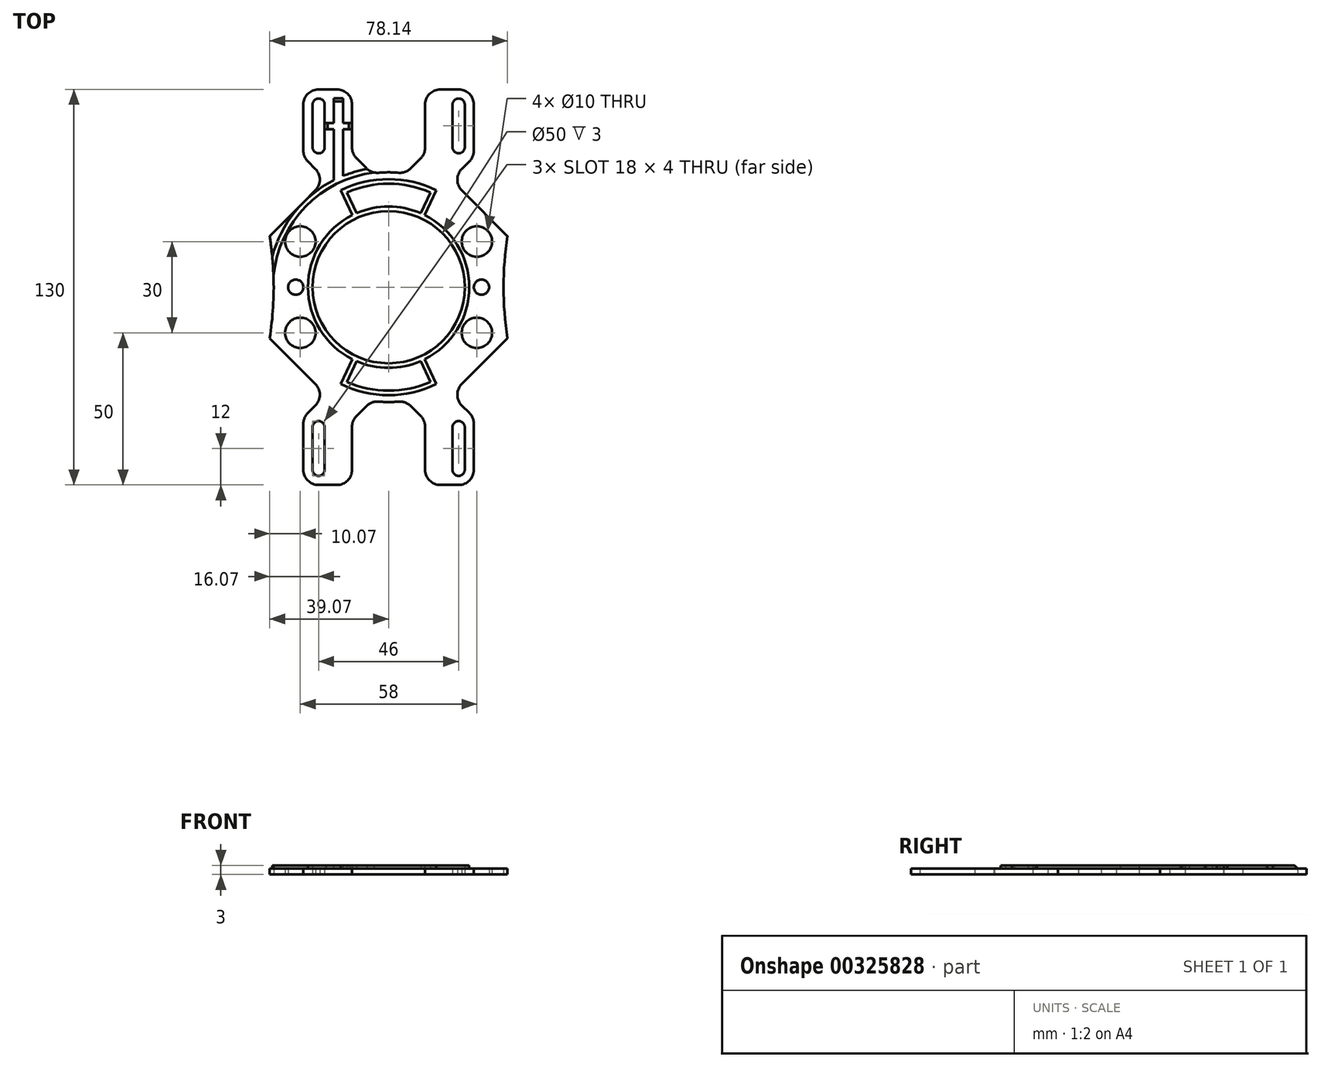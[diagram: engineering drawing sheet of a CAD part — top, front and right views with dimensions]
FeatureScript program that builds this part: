
annotation { "Feature Type Name" : "Feature", "Feature Type Description" : "" }
export const myFeature = defineFeature(function(context is Context, id is Id, definition is map)
    precondition{}
    {
        {
            var Q0;
            Q0=qCreatedBy(makeId("Top.planeOp"),FACE);
            var sketch = newSketch(context, id + "F0", { "sketchPlane" : qUnion([Q0])});
            skLineSegment(sketch, "E0.left", {"start": v(-2, 12.5) * mm, "end": v(-2, -12.5) * mm});
            skLineSegment(sketch, "E0.right", {"start": v(2, 12.5) * mm, "end": v(2, -12.5) * mm});
            skLineSegment(sketch, "E1", {"start": v(0, 0) * mm, "end": v(0, 81.3) * mm, "construction": true});
            skArc(sketch, "E2", {"start": v(2, 12.5) * mm, "mid": v(0, 14.5) * mm, "end": v(-2, 12.5) * mm});
            skArc(sketch, "E3", {"start": v(-2, -12.5) * mm, "mid": v(0, -14.5) * mm, "end": v(2, -12.5) * mm});
            skLineSegment(sketch, "E4", {"start": v(-106.98, 0) * mm, "end": v(54.3, 0) * mm, "construction": true});
            skLineSegment(sketch, "E5.left", {"start": v(-19, 9) * mm, "end": v(-19, -9) * mm});
            skLineSegment(sketch, "E5.right", {"start": v(-15, 9) * mm, "end": v(-15, -9) * mm});
            skArc(sketch, "E6", {"start": v(-15, 9) * mm, "mid": v(-17, 11) * mm, "end": v(-19, 9) * mm});
            skArc(sketch, "E7", {"start": v(-19, -9) * mm, "mid": v(-17, -11) * mm, "end": v(-15, -9) * mm});
            skArc(sketch, "E8.MirrorCS", {"start": v(19, -9) * mm, "mid": v(17, -11) * mm, "end": v(15, -9) * mm});
            skArc(sketch, "E9.MirrorCS", {"start": v(15, 9) * mm, "mid": v(17, 11) * mm, "end": v(19, 9) * mm});
            skLineSegment(sketch, "E10.MirrorCS", {"start": v(15, 9) * mm, "end": v(15, -9) * mm});
            skLineSegment(sketch, "E11.MirrorCS", {"start": v(19, 9) * mm, "end": v(19, -9) * mm});
            skCircle(sketch, "E12", {"center": v(-30.5, 0) * mm, "radius": 2.5 * mm});
            skCircle(sketch, "E13.MirrorC", {"center": v(30.5, 0) * mm, "radius": 2.5 * mm});
            skCircle(sketch, "E14", {"center": v(0, 29) * mm, "radius": 7.5 * mm});
            skCircle(sketch, "E15.MirrorC", {"center": v(0, -29) * mm, "radius": 7.5 * mm});
            skCircle(sketch, "E16", {"center": v(-29, 15) * mm, "radius": 5 * mm});
            skCircle(sketch, "E17.MirrorC", {"center": v(29, 15) * mm, "radius": 5 * mm});
            skCircle(sketch, "E18.MirrorC", {"center": v(-29, -15) * mm, "radius": 5 * mm});
            skCircle(sketch, "E19.MirrorC", {"center": v(29, -15) * mm, "radius": 5 * mm});
            skLineSegment(sketch, "E20.bottom", {"start": v(-4.5, 44) * mm, "end": v(4.5, 44) * mm});
            skLineSegment(sketch, "E20.top", {"start": v(-4.5, 42) * mm, "end": v(4.5, 42) * mm});
            skLineSegment(sketch, "E20.left", {"start": v(-4.5, 44) * mm, "end": v(-4.5, 42) * mm, "construction": true});
            skLineSegment(sketch, "E20.right", {"start": v(4.5, 44) * mm, "end": v(4.5, 42) * mm, "construction": true});
            skArc(sketch, "E21", {"start": v(-4.5, 44) * mm, "mid": v(-5.5, 43) * mm, "end": v(-4.5, 42) * mm});
            skArc(sketch, "E22", {"start": v(4.5, 42) * mm, "mid": v(5.5, 43) * mm, "end": v(4.5, 44) * mm});
            skLineSegment(sketch, "E23", {"start": v(-11.75, 47.5) * mm, "end": v(11.75, 47.5) * mm});
            skLineSegment(sketch, "E24", {"start": v(-18, -65) * mm, "end": v(18, -65) * mm});
            skArc(sketch, "E25", {"start": v(-41, -26.18) * mm, "mid": v(-37.75, 0) * mm, "end": v(-41, 26.18) * mm});
            skLineSegment(sketch, "E26", {"start": v(-41, 26.18) * mm, "end": v(-26.18, 41) * mm});
            skLineSegment(sketch, "E27", {"start": v(-26.18, 41) * mm, "end": v(-17.75, 41) * mm});
            skLineSegment(sketch, "E28", {"start": v(-17.75, 41) * mm, "end": v(-11.75, 47.5) * mm});
            skLineSegment(sketch, "E29", {"start": v(0, 0) * mm, "end": v(-64.55, 64.55) * mm, "construction": true});
            skLineSegment(sketch, "E30.MirrorCS", {"start": v(-41, -26.18) * mm, "end": v(-26.18, -41) * mm});
            skLineSegment(sketch, "E31", {"start": v(-18, -65) * mm, "end": v(-18, -41) * mm});
            skLineSegment(sketch, "E32", {"start": v(-18, -41) * mm, "end": v(-26.18, -41) * mm});
            skLineSegment(sketch, "E33.MirrorCS", {"start": v(41, 26.18) * mm, "end": v(26.18, 41) * mm});
            skLineSegment(sketch, "E34.MirrorCS", {"start": v(26.18, 41) * mm, "end": v(17.75, 41) * mm});
            skLineSegment(sketch, "E35.MirrorCS", {"start": v(17.75, 41) * mm, "end": v(11.75, 47.5) * mm});
            skArc(sketch, "E36.MirrorCS", {"start": v(41, -26.18) * mm, "mid": v(37.75, 0) * mm, "end": v(41, 26.18) * mm});
            skLineSegment(sketch, "E37.MirrorCS", {"start": v(41, -26.18) * mm, "end": v(26.18, -41) * mm});
            skLineSegment(sketch, "E38.MirrorCS", {"start": v(18, -41) * mm, "end": v(26.18, -41) * mm});
            skLineSegment(sketch, "E39.MirrorCS", {"start": v(18, -65) * mm, "end": v(18, -41) * mm});
            skCircle(sketch, "E40", {"center": v(-26.16, 36.77) * mm, "radius": 1.63 * mm});
            skCircle(sketch, "E41", {"center": v(-36.77, 26.16) * mm, "radius": 1.63 * mm});
            skLineSegment(sketch, "E42", {"start": v(-21.93, 41) * mm, "end": v(-40.2, 22.74) * mm, "construction": true});
            skCircle(sketch, "E43.1.0", {"center": v(-36.77, -26.16) * mm, "radius": 1.63 * mm});
            skCircle(sketch, "E43.1.1", {"center": v(-26.16, -36.77) * mm, "radius": 1.63 * mm});
            skCircle(sketch, "E43.2.0", {"center": v(26.16, -36.77) * mm, "radius": 1.63 * mm});
            skCircle(sketch, "E43.2.1", {"center": v(36.77, -26.16) * mm, "radius": 1.63 * mm});
            skCircle(sketch, "E43.3.0", {"center": v(36.77, 26.16) * mm, "radius": 1.63 * mm});
            skCircle(sketch, "E43.3.1", {"center": v(26.16, 36.77) * mm, "radius": 1.63 * mm});
            skPoint(sketch, "E43.center", {"position": v(0, 0) * mm});
            skSolve(sketch);
        }
        {
            var Q0;
            Q0=qCreatedBy(makeId("Top.planeOp"),FACE);
            var sketch = newSketch(context, id + "F1", { "sketchPlane" : qUnion([Q0])});
            skCircle(sketch, "E44.0", {"center": v(-30.5, 0) * mm, "radius": 2.5 * mm});
            skCircle(sketch, "E45.0", {"center": v(30.5, 0) * mm, "radius": 2.5 * mm});
            skCircle(sketch, "E46.0", {"center": v(-29, -15) * mm, "radius": 5 * mm});
            skPoint(sketch, "E47.0", {"position": v(-33.59, -33.59) * mm});
            skLineSegment(sketch, "E48.0", {"start": v(-41, -26.18) * mm, "end": v(-26.18, -41) * mm, "construction": true});
            skPoint(sketch, "E49.0", {"position": v(-22.09, -41) * mm});
            skArc(sketch, "E50.0.6", {"start": v(39.07, -16.79) * mm, "mid": v(38.08, -8.42) * mm, "end": v(37.75, 0) * mm});
            skArc(sketch, "E50.0.14", {"start": v(-37.75, 0) * mm, "mid": v(-38.08, -8.42) * mm, "end": v(-39.07, -16.79) * mm});
            skLineSegment(sketch, "E51", {"start": v(-28, -65) * mm, "end": v(-12, -65) * mm});
            skLineSegment(sketch, "E52", {"start": v(-39.07, -16.79) * mm, "end": v(-20.52, -35.34) * mm});
            skLineSegment(sketch, "E53", {"start": v(-28, -42.82) * mm, "end": v(-20.52, -35.34) * mm});
            skLineSegment(sketch, "E54.MirrorCS", {"start": v(39.07, -16.79) * mm, "end": v(20.52, -35.34) * mm});
            skPoint(sketch, "E55.orphan", {"position": v(41, -26.18) * mm});
            skLineSegment(sketch, "E56", {"start": v(37.75, 0) * mm, "end": v(-37.75, 0) * mm, "construction": true});
            skPoint(sketch, "E57.orphan", {"position": v(-41, -26.18) * mm});
            skPoint(sketch, "E58.MirrorP", {"position": v(-41, 26.18) * mm});
            skLineSegment(sketch, "E59.MirrorCS", {"start": v(39.07, 16.79) * mm, "end": v(20.52, 35.34) * mm});
            skPoint(sketch, "E60.MirrorP", {"position": v(-33.59, 33.59) * mm});
            skPoint(sketch, "E61.MirrorP", {"position": v(-22.09, 41) * mm});
            skLineSegment(sketch, "E62.MirrorCS", {"start": v(-39.07, 16.79) * mm, "end": v(-20.52, 35.34) * mm});
            skPoint(sketch, "E63.MirrorP", {"position": v(41, 26.18) * mm});
            skLineSegment(sketch, "E64.MirrorCS", {"start": v(-41, 26.18) * mm, "end": v(-26.18, 41) * mm, "construction": true});
            skCircle(sketch, "E65.MirrorC", {"center": v(-29, 15) * mm, "radius": 5 * mm});
            skArc(sketch, "E66.MirrorCS", {"start": v(39.07, 16.79) * mm, "mid": v(38.08, 8.42) * mm, "end": v(37.75, 0) * mm});
            skArc(sketch, "E67.MirrorCS", {"start": v(-37.75, 0) * mm, "mid": v(-38.08, 8.42) * mm, "end": v(-39.07, 16.79) * mm});
            skLineSegment(sketch, "E68.bottom", {"start": v(-25, -46) * mm, "end": v(-21, -46) * mm});
            skLineSegment(sketch, "E68.top", {"start": v(-25, -60) * mm, "end": v(-21, -60) * mm});
            skLineSegment(sketch, "E68.left", {"start": v(-25, -46) * mm, "end": v(-25, -60) * mm});
            skLineSegment(sketch, "E68.right", {"start": v(-21, -46) * mm, "end": v(-21, -60) * mm});
            skArc(sketch, "E69", {"start": v(-21, -46) * mm, "mid": v(-23, -44) * mm, "end": v(-25, -46) * mm});
            skArc(sketch, "E70", {"start": v(-25, -60) * mm, "mid": v(-23, -62) * mm, "end": v(-21, -60) * mm});
            skLineSegment(sketch, "E71.0", {"start": v(19, 9) * mm, "end": v(19, -9) * mm});
            skLineSegment(sketch, "E71.1", {"start": v(-2, 12.5) * mm, "end": v(-2, -12.5) * mm});
            skLineSegment(sketch, "E71.2", {"start": v(2, 12.5) * mm, "end": v(2, -12.5) * mm});
            skArc(sketch, "E71.3", {"start": v(2, 12.5) * mm, "mid": v(0, 14.5) * mm, "end": v(-2, 12.5) * mm});
            skLineSegment(sketch, "E71.4", {"start": v(-19, 9) * mm, "end": v(-19, -9) * mm});
            skLineSegment(sketch, "E71.5", {"start": v(-15, 9) * mm, "end": v(-15, -9) * mm});
            skArc(sketch, "E71.6", {"start": v(-15, 9) * mm, "mid": v(-17, 11) * mm, "end": v(-19, 9) * mm});
            skArc(sketch, "E71.7", {"start": v(-19, -9) * mm, "mid": v(-17, -11) * mm, "end": v(-15, -9) * mm});
            skArc(sketch, "E71.8", {"start": v(19, -9) * mm, "mid": v(17, -11) * mm, "end": v(15, -9) * mm});
            skArc(sketch, "E71.9", {"start": v(15, 9) * mm, "mid": v(17, 11) * mm, "end": v(19, 9) * mm});
            skLineSegment(sketch, "E71.10", {"start": v(15, 9) * mm, "end": v(15, -9) * mm});
            skArc(sketch, "E72.0", {"start": v(-2, -12.5) * mm, "mid": v(0, -14.5) * mm, "end": v(2, -12.5) * mm});
            skCircle(sketch, "E73", {"center": v(0, 0) * mm, "radius": 25 * mm});
            skPoint(sketch, "E74.orphan", {"position": v(20.52, 35.34) * mm});
            skPoint(sketch, "E75.orphan", {"position": v(20.52, -35.34) * mm});
            skArc(sketch, "E76.trimOffspring", {"start": v(-5.55, -37.34) * mm, "mid": v(0, -37.75) * mm, "end": v(5.55, -37.34) * mm});
            skLineSegment(sketch, "E77", {"start": v(-12, -65) * mm, "end": v(-12, -43.8) * mm});
            skLineSegment(sketch, "E78", {"start": v(-12, -43.8) * mm, "end": v(-5.55, -37.34) * mm});
            skLineSegment(sketch, "E79", {"start": v(0, 0) * mm, "end": v(0, 32.65) * mm, "construction": true});
            skCircle(sketch, "E80", {"center": v(0, 0) * mm, "radius": 32.65 * mm, "construction": true});
            skLineSegment(sketch, "E81", {"start": v(-28, -42.82) * mm, "end": v(-28, -65) * mm});
            skPoint(sketch, "E82.orphan", {"position": v(-18, -65) * mm});
            skLineSegment(sketch, "E83.0", {"start": v(-18, -65) * mm, "end": v(-18, -41) * mm, "construction": true});
            skLineSegment(sketch, "E84", {"start": v(-18, -53) * mm, "end": v(-28, -53) * mm, "construction": true});
            skLineSegment(sketch, "E85", {"start": v(-23, -53) * mm, "end": v(-23, -65) * mm, "construction": true});
            skLineSegment(sketch, "E86.MirrorCS", {"start": v(12, -43.8) * mm, "end": v(5.55, -37.34) * mm});
            skLineSegment(sketch, "E87.MirrorCS", {"start": v(28, -42.82) * mm, "end": v(20.52, -35.34) * mm});
            skLineSegment(sketch, "E88.MirrorCS", {"start": v(28, -42.82) * mm, "end": v(28, -65) * mm});
            skLineSegment(sketch, "E89.MirrorCS", {"start": v(12, -65) * mm, "end": v(12, -43.8) * mm});
            skLineSegment(sketch, "E90.MirrorCS", {"start": v(28, -65) * mm, "end": v(12, -65) * mm});
            skArc(sketch, "E91.MirrorCS", {"start": v(25, -60) * mm, "mid": v(23, -62) * mm, "end": v(21, -60) * mm});
            skLineSegment(sketch, "E92.MirrorCS", {"start": v(21, -46) * mm, "end": v(21, -60) * mm});
            skArc(sketch, "E93.MirrorCS", {"start": v(21, -46) * mm, "mid": v(23, -44) * mm, "end": v(25, -46) * mm});
            skLineSegment(sketch, "E94.MirrorCS", {"start": v(25, -46) * mm, "end": v(25, -60) * mm});
            skLineSegment(sketch, "E95.MirrorCS", {"start": v(28, 42.82) * mm, "end": v(20.52, 35.34) * mm});
            skLineSegment(sketch, "E96.MirrorCS", {"start": v(12, 43.8) * mm, "end": v(5.55, 37.34) * mm});
            skLineSegment(sketch, "E97.MirrorCS", {"start": v(-12, 43.8) * mm, "end": v(-5.55, 37.34) * mm});
            skLineSegment(sketch, "E98.MirrorCS", {"start": v(-28, 42.82) * mm, "end": v(-20.52, 35.34) * mm});
            skLineSegment(sketch, "E99.MirrorCS", {"start": v(-12, 65) * mm, "end": v(-12, 43.8) * mm});
            skLineSegment(sketch, "E100.MirrorCS", {"start": v(12, 65) * mm, "end": v(12, 43.8) * mm});
            skLineSegment(sketch, "E101.MirrorCS", {"start": v(28, 42.82) * mm, "end": v(28, 65) * mm});
            skLineSegment(sketch, "E102.MirrorCS", {"start": v(28, 65) * mm, "end": v(12, 65) * mm});
            skLineSegment(sketch, "E103.MirrorCS", {"start": v(-28, 65) * mm, "end": v(-12, 65) * mm});
            skLineSegment(sketch, "E104.MirrorCS", {"start": v(-28, 42.82) * mm, "end": v(-28, 65) * mm});
            skLineSegment(sketch, "E105.MirrorCS", {"start": v(-25, 46) * mm, "end": v(-25, 60) * mm});
            skLineSegment(sketch, "E106.MirrorCS", {"start": v(-21, 46) * mm, "end": v(-21, 60) * mm});
            skArc(sketch, "E107.MirrorCS", {"start": v(-21, 46) * mm, "mid": v(-23, 44) * mm, "end": v(-25, 46) * mm});
            skArc(sketch, "E108.MirrorCS", {"start": v(21, 46) * mm, "mid": v(23, 44) * mm, "end": v(25, 46) * mm});
            skLineSegment(sketch, "E109.MirrorCS", {"start": v(25, 46) * mm, "end": v(25, 60) * mm});
            skLineSegment(sketch, "E110.MirrorCS", {"start": v(21, 46) * mm, "end": v(21, 60) * mm});
            skArc(sketch, "E111.MirrorCS", {"start": v(25, 60) * mm, "mid": v(23, 62) * mm, "end": v(21, 60) * mm});
            skArc(sketch, "E112.MirrorCS", {"start": v(-25, 60) * mm, "mid": v(-23, 62) * mm, "end": v(-21, 60) * mm});
            skArc(sketch, "E113.trimOffspring", {"start": v(5.55, 37.34) * mm, "mid": v(0, 37.75) * mm, "end": v(-5.55, 37.34) * mm});
            skCircle(sketch, "E114.0", {"center": v(29, 15) * mm, "radius": 5 * mm});
            skCircle(sketch, "E115.0", {"center": v(29, -15) * mm, "radius": 5 * mm});
            skLineSegment(sketch, "E116", {"start": v(0, -37.75) * mm, "end": v(0, 37.75) * mm, "construction": true});
            skSolve(sketch);
        }
        {
            var Q0;
            Q0=makeQuery(id+"F1.imprint","IMPRINT",FACE,{"disambiguationData":[TD([[makeQuery(id+"F1.imprint","IMPRINT",EDGE,{"derivedFrom":sQuery(id+"F1.wireOp",EDGE,"E44.0")}),-1.0]])]});
            extrude(context, id + "F2", {"entities" : qUnion([Q0]), "depth" : 2 * mm});
        }
        {
            var Q0;
            Q0=makeQuery(id+"F2.opExtrude","SWEPT_EDGE",EDGE,{"disambiguationData":[OSD([sQuery(id+"F1.wireOp",EDGE,"E103.MirrorCS"),sQuery(id+"F1.wireOp",EDGE,"E104.MirrorCS")])]});
            var Q1;
            Q1=makeQuery(id+"F2.opExtrude","SWEPT_EDGE",EDGE,{"disambiguationData":[OSD([sQuery(id+"F1.wireOp",EDGE,"E99.MirrorCS"),sQuery(id+"F1.wireOp",EDGE,"E103.MirrorCS")])]});
            var Q2;
            Q2=makeQuery(id+"F2.opExtrude","SWEPT_EDGE",EDGE,{"disambiguationData":[OSD([sQuery(id+"F1.wireOp",EDGE,"E101.MirrorCS"),sQuery(id+"F1.wireOp",EDGE,"E102.MirrorCS")])]});
            var Q3;
            Q3=makeQuery(id+"F2.opExtrude","SWEPT_EDGE",EDGE,{"disambiguationData":[OSD([sQuery(id+"F1.wireOp",EDGE,"E100.MirrorCS"),sQuery(id+"F1.wireOp",EDGE,"E102.MirrorCS")])]});
            var Q4;
            Q4=makeQuery(id+"F2.opExtrude","SWEPT_EDGE",EDGE,{"disambiguationData":[OSD([sQuery(id+"F1.wireOp",EDGE,"E51"),sQuery(id+"F1.wireOp",EDGE,"E77")])]});
            var Q5;
            Q5=makeQuery(id+"F2.opExtrude","SWEPT_EDGE",EDGE,{"disambiguationData":[OSD([sQuery(id+"F1.wireOp",EDGE,"E89.MirrorCS"),sQuery(id+"F1.wireOp",EDGE,"E90.MirrorCS")])]});
            var Q6;
            Q6=makeQuery(id+"F2.opExtrude","SWEPT_EDGE",EDGE,{"disambiguationData":[OSD([sQuery(id+"F1.wireOp",EDGE,"E88.MirrorCS"),sQuery(id+"F1.wireOp",EDGE,"E90.MirrorCS")])]});
            var Q7;
            Q7=makeQuery(id+"F2.opExtrude","SWEPT_EDGE",EDGE,{"disambiguationData":[OSD([sQuery(id+"F1.wireOp",EDGE,"E51"),sQuery(id+"F1.wireOp",EDGE,"E81")])]});
            var Q8;
            Q8=makeQuery(id+"F2.opExtrude","SWEPT_EDGE",EDGE,{"disambiguationData":[OSD([sQuery(id+"F1.wireOp",EDGE,"E98.MirrorCS"),sQuery(id+"F1.wireOp",EDGE,"E104.MirrorCS")])]});
            var Q9;
            Q9=makeQuery(id+"F2.opExtrude","SWEPT_EDGE",EDGE,{"disambiguationData":[OSD([sQuery(id+"F1.wireOp",EDGE,"E95.MirrorCS"),sQuery(id+"F1.wireOp",EDGE,"E101.MirrorCS")])]});
            var Q10;
            Q10=makeQuery(id+"F2.opExtrude","SWEPT_EDGE",EDGE,{"disambiguationData":[OSD([sQuery(id+"F1.wireOp",EDGE,"E87.MirrorCS"),sQuery(id+"F1.wireOp",EDGE,"E88.MirrorCS")])]});
            var Q11;
            Q11=makeQuery(id+"F2.opExtrude","SWEPT_EDGE",EDGE,{"disambiguationData":[OSD([sQuery(id+"F1.wireOp",EDGE,"E53"),sQuery(id+"F1.wireOp",EDGE,"E81")])]});
            var Q12;
            Q12=makeQuery(id+"F2.opExtrude","SWEPT_EDGE",EDGE,{"disambiguationData":[OSD([sQuery(id+"F1.wireOp",EDGE,"E77"),sQuery(id+"F1.wireOp",EDGE,"E78")])]});
            var Q13;
            Q13=makeQuery(id+"F2.opExtrude","SWEPT_EDGE",EDGE,{"disambiguationData":[OSD([sQuery(id+"F1.wireOp",EDGE,"E76.trimOffspring"),sQuery(id+"F1.wireOp",EDGE,"E78")])]});
            var Q14;
            Q14=makeQuery(id+"F2.opExtrude","SWEPT_EDGE",EDGE,{"disambiguationData":[OSD([sQuery(id+"F1.wireOp",EDGE,"E76.trimOffspring"),sQuery(id+"F1.wireOp",EDGE,"E86.MirrorCS")])]});
            var Q15;
            Q15=makeQuery(id+"F2.opExtrude","SWEPT_EDGE",EDGE,{"disambiguationData":[OSD([sQuery(id+"F1.wireOp",EDGE,"E86.MirrorCS"),sQuery(id+"F1.wireOp",EDGE,"E89.MirrorCS")])]});
            var Q16;
            Q16=makeQuery(id+"F2.opExtrude","SWEPT_EDGE",EDGE,{"disambiguationData":[OSD([sQuery(id+"F1.wireOp",EDGE,"E87.MirrorCS"),sQuery(id+"F1.wireOp",EDGE,"7007121e-37ec-4c2c-a8ca-d383ff4ec926.trimOffspring")])]});
            var Q17;
            Q17=makeQuery(id+"F2.opExtrude","SWEPT_EDGE",EDGE,{"disambiguationData":[OSD([sQuery(id+"F1.wireOp",EDGE,"E53"),sQuery(id+"F1.wireOp",EDGE,"26zSKZWf-6ghU-qzgI-eylg-SGAcErsO0g6f")])]});
            var Q18;
            Q18=makeQuery(id+"F2.opExtrude","SWEPT_EDGE",EDGE,{"disambiguationData":[OSD([sQuery(id+"F1.wireOp",EDGE,"E98.MirrorCS"),sQuery(id+"F1.wireOp",EDGE,"ae5d58c6-9cf7-4faf-a310-24e2495b33ea.trimOffspring")])]});
            var Q19;
            Q19=makeQuery(id+"F2.opExtrude","SWEPT_EDGE",EDGE,{"disambiguationData":[OSD([sQuery(id+"F1.wireOp",EDGE,"E97.MirrorCS"),sQuery(id+"F1.wireOp",EDGE,"E99.MirrorCS")])]});
            var Q20;
            Q20=makeQuery(id+"F2.opExtrude","SWEPT_EDGE",EDGE,{"disambiguationData":[OSD([sQuery(id+"F1.wireOp",EDGE,"E97.MirrorCS"),sQuery(id+"F1.wireOp",EDGE,"E113.trimOffspring")])]});
            var Q21;
            Q21=makeQuery(id+"F2.opExtrude","SWEPT_EDGE",EDGE,{"disambiguationData":[OSD([sQuery(id+"F1.wireOp",EDGE,"E96.MirrorCS"),sQuery(id+"F1.wireOp",EDGE,"E113.trimOffspring")])]});
            var Q22;
            Q22=makeQuery(id+"F2.opExtrude","SWEPT_EDGE",EDGE,{"disambiguationData":[OSD([sQuery(id+"F1.wireOp",EDGE,"E96.MirrorCS"),sQuery(id+"F1.wireOp",EDGE,"E100.MirrorCS")])]});
            var Q23;
            Q23=makeQuery(id+"F2.opExtrude","SWEPT_EDGE",EDGE,{"disambiguationData":[OSD([sQuery(id+"F1.wireOp",EDGE,"7007121e-37ec-4c2c-a8ca-d383ff4ec926.trimOffspring"),sQuery(id+"F1.wireOp",EDGE,"E95.MirrorCS")])]});
            fillet(context, id + "F3", {"entities" : qUnion([Q0, Q1, Q2, Q3, Q4, Q5, Q6, Q7, Q8, Q9, Q10, Q11, Q12, Q13, Q14, Q15, Q16, Q17, Q18, Q19, Q20, Q21, Q22, Q23]), "radius" : 5 * mm, "tangentPropagation" : true, "allowEdgeOverflow" : false});
        }
        {
            var Q0;
            Q0=makeQuery(id+"F2.opExtrude","CAP_FACE",FACE,{"disambiguationData":[OSD([sQuery(id+"F1.wireOp",EDGE,"E44.0"),sQuery(id+"F1.wireOp",EDGE,"E45.0"),sQuery(id+"F1.wireOp",EDGE,"E46.0"),sQuery(id+"F1.wireOp",EDGE,"E50.0.6"),sQuery(id+"F1.wireOp",EDGE,"E50.0.14"),sQuery(id+"F1.wireOp",EDGE,"E51"),sQuery(id+"F1.wireOp",EDGE,"E52"),sQuery(id+"F1.wireOp",EDGE,"E53"),sQuery(id+"F1.wireOp",EDGE,"E54.MirrorCS"),sQuery(id+"F1.wireOp",EDGE,"E59.MirrorCS"),sQuery(id+"F1.wireOp",EDGE,"E62.MirrorCS"),sQuery(id+"F1.wireOp",EDGE,"E65.MirrorC"),sQuery(id+"F1.wireOp",EDGE,"E66.MirrorCS"),sQuery(id+"F1.wireOp",EDGE,"E67.MirrorCS"),sQuery(id+"F1.wireOp",EDGE,"E68.left"),sQuery(id+"F1.wireOp",EDGE,"E68.right"),sQuery(id+"F1.wireOp",EDGE,"E69"),sQuery(id+"F1.wireOp",EDGE,"E70"),sQuery(id+"F1.wireOp",EDGE,"E73"),sQuery(id+"F1.wireOp",EDGE,"E76.trimOffspring"),sQuery(id+"F1.wireOp",EDGE,"E77"),sQuery(id+"F1.wireOp",EDGE,"E78"),sQuery(id+"F1.wireOp",EDGE,"E81"),sQuery(id+"F1.wireOp",EDGE,"E86.MirrorCS"),sQuery(id+"F1.wireOp",EDGE,"E87.MirrorCS"),sQuery(id+"F1.wireOp",EDGE,"E88.MirrorCS"),sQuery(id+"F1.wireOp",EDGE,"E89.MirrorCS"),sQuery(id+"F1.wireOp",EDGE,"E90.MirrorCS"),sQuery(id+"F1.wireOp",EDGE,"E91.MirrorCS"),sQuery(id+"F1.wireOp",EDGE,"E92.MirrorCS"),sQuery(id+"F1.wireOp",EDGE,"E93.MirrorCS"),sQuery(id+"F1.wireOp",EDGE,"E94.MirrorCS"),sQuery(id+"F1.wireOp",EDGE,"E95.MirrorCS"),sQuery(id+"F1.wireOp",EDGE,"E96.MirrorCS"),sQuery(id+"F1.wireOp",EDGE,"E97.MirrorCS"),sQuery(id+"F1.wireOp",EDGE,"E98.MirrorCS"),sQuery(id+"F1.wireOp",EDGE,"E99.MirrorCS"),sQuery(id+"F1.wireOp",EDGE,"E100.MirrorCS"),sQuery(id+"F1.wireOp",EDGE,"E101.MirrorCS"),sQuery(id+"F1.wireOp",EDGE,"E102.MirrorCS"),sQuery(id+"F1.wireOp",EDGE,"E103.MirrorCS"),sQuery(id+"F1.wireOp",EDGE,"E104.MirrorCS"),sQuery(id+"F1.wireOp",EDGE,"E105.MirrorCS"),sQuery(id+"F1.wireOp",EDGE,"E106.MirrorCS"),sQuery(id+"F1.wireOp",EDGE,"E107.MirrorCS"),sQuery(id+"F1.wireOp",EDGE,"E108.MirrorCS"),sQuery(id+"F1.wireOp",EDGE,"E109.MirrorCS"),sQuery(id+"F1.wireOp",EDGE,"E110.MirrorCS"),sQuery(id+"F1.wireOp",EDGE,"E111.MirrorCS"),sQuery(id+"F1.wireOp",EDGE,"E112.MirrorCS"),sQuery(id+"F1.wireOp",EDGE,"E113.trimOffspring"),sQuery(id+"F1.wireOp",EDGE,"E114.0"),sQuery(id+"F1.wireOp",EDGE,"E115.0")])],"isStart":false});
            var sketch = newSketch(context, id + "F4", { "sketchPlane" : qUnion([Q0])});
            skLineSegment(sketch, "E117.bottom", {"start": v(-18, 62) * mm, "end": v(-15, 62) * mm});
            skLineSegment(sketch, "E117.left", {"start": v(-18, 62) * mm, "end": v(-18, 53.93) * mm});
            skLineSegment(sketch, "E117.right", {"start": v(-15, 62) * mm, "end": v(-15, 53.93) * mm});
            skLineSegment(sketch, "E118", {"start": v(-12, 52.93) * mm, "end": v(-21, 52.93) * mm, "construction": true});
            skLineSegment(sketch, "E119", {"start": v(-16.5, 52.93) * mm, "end": v(-16.5, 68.87) * mm, "construction": true});
            skLineSegment(sketch, "E120", {"start": v(0, 0) * mm, "end": v(0, 37.75) * mm, "construction": true});
            skLineSegment(sketch, "E121", {"start": v(-37.8, 0) * mm, "end": v(37.75, 0) * mm, "construction": true});
            skCircle(sketch, "E122", {"center": v(0, 0) * mm, "radius": 37.8 * mm, "construction": true});
            skLineSegment(sketch, "E123.0", {"start": v(-12, 53.93) * mm, "end": v(-16.5, 53.93) * mm});
            skLineSegment(sketch, "E124.MirrorCS", {"start": v(-12, 51.93) * mm, "end": v(-15, 51.93) * mm});
            skLineSegment(sketch, "E125", {"start": v(-21, 53.93) * mm, "end": v(-21, 51.93) * mm});
            skLineSegment(sketch, "E126.0", {"start": v(-21, 46) * mm, "end": v(-21, 60) * mm, "construction": true});
            skLineSegment(sketch, "E127", {"start": v(-12, 53.93) * mm, "end": v(-12, 51.93) * mm});
            skLineSegment(sketch, "E128.0", {"start": v(-12, 60) * mm, "end": v(-12, 45.87) * mm, "construction": true});
            skLineSegment(sketch, "E129.trimOffspring", {"start": v(-18, 53.93) * mm, "end": v(-21, 53.93) * mm});
            skLineSegment(sketch, "E130.trimOffspring", {"start": v(-18, 51.93) * mm, "end": v(-18, 35.16) * mm});
            skLineSegment(sketch, "E131.trimOffspring", {"start": v(-18, 51.93) * mm, "end": v(-21, 51.93) * mm});
            skLineSegment(sketch, "E132.trimOffspring", {"start": v(-15, 51.93) * mm, "end": v(-15, 36.54) * mm});
            skCircle(sketch, "E133", {"center": v(0, 0) * mm, "radius": 36.3 * mm, "construction": true});
            skArc(sketch, "E134.0", {"start": v(-4.77, 37.7) * mm, "mid": v(-27.23, 26.5) * mm, "end": v(-37.82, 3.74) * mm});
            skArc(sketch, "E135.0", {"start": v(-7.06, 38.86) * mm, "mid": v(-11.1, 37.91) * mm, "end": v(-15, 36.54) * mm});
            skArc(sketch, "E136.0", {"start": v(-3.29, 37.6) * mm, "mid": v(-5.3, 37.84) * mm, "end": v(-7.06, 38.86) * mm});
            skPoint(sketch, "E137.orphan", {"position": v(-7.26, 39.05) * mm});
            skArc(sketch, "E138.0", {"start": v(-38.22, 9.99) * mm, "mid": v(-37.97, 6.87) * mm, "end": v(-37.82, 3.74) * mm});
            skArc(sketch, "E139.trimOffspring", {"start": v(-18, 35.16) * mm, "mid": v(-30.8, 24.73) * mm, "end": v(-38.22, 9.99) * mm});
            skPoint(sketch, "E140.orphan", {"position": v(-39.07, 16.79) * mm});
            skPoint(sketch, "E141.orphan", {"position": v(-39.07, -16.79) * mm});
            skCircle(sketch, "E142.0", {"center": v(0, 0) * mm, "radius": 25 * mm});
            skArc(sketch, "E143.0", {"start": v(-11.87, 23.7) * mm, "mid": v(-26.5, 0) * mm, "end": v(-11.87, -23.7) * mm});
            skLineSegment(sketch, "E144", {"start": v(0, 0) * mm, "end": v(-22.55, 48.35) * mm, "construction": true});
            skLineSegment(sketch, "E145.trimOffspring", {"start": v(-10.52, 24.32) * mm, "end": v(-13.68, 31.12) * mm});
            skLineSegment(sketch, "E146.trimOffspring", {"start": v(-11.87, 23.7) * mm, "end": v(-15.68, 31.85) * mm});
            skLineSegment(sketch, "E147.MirrorCS", {"start": v(10.52, 24.32) * mm, "end": v(13.68, 31.12) * mm});
            skLineSegment(sketch, "E148.MirrorCS", {"start": v(11.87, 23.7) * mm, "end": v(15.68, 31.85) * mm});
            skArc(sketch, "E149.MirrorCS", {"start": v(4.77, 37.7) * mm, "mid": v(27.23, 26.5) * mm, "end": v(37.82, 3.74) * mm});
            skArc(sketch, "E150.trimOffspring", {"start": v(10.52, 24.32) * mm, "mid": v(0, 26.5) * mm, "end": v(-10.52, 24.32) * mm});
            skArc(sketch, "E151.MirrorCS", {"start": v(-4.77, -37.7) * mm, "mid": v(-27.23, -26.5) * mm, "end": v(-37.82, -3.74) * mm});
            skArc(sketch, "E152.trimOffspring", {"start": v(-10.52, -24.32) * mm, "mid": v(0, -26.5) * mm, "end": v(10.52, -24.32) * mm});
            skArc(sketch, "E153.trimOffspring", {"start": v(11.87, -23.7) * mm, "mid": v(26.5, 0) * mm, "end": v(11.87, 23.7) * mm});
            skPoint(sketch, "E154.trimOffspring.end.orphan", {"position": v(-16.74, 34.12) * mm});
            skPoint(sketch, "E155.trimOffspring.end.orphan", {"position": v(-15.38, 34.75) * mm});
            skPoint(sketch, "E156.orphan", {"position": v(15.38, 34.75) * mm});
            skPoint(sketch, "E157.orphan", {"position": v(16.74, 34.12) * mm});
            skArc(sketch, "E158", {"start": v(15.68, 31.85) * mm, "mid": v(0, 35.5) * mm, "end": v(-15.68, 31.85) * mm});
            skArc(sketch, "E159.0", {"start": v(13.68, 31.12) * mm, "mid": v(0, 34) * mm, "end": v(-13.68, 31.12) * mm});
            skLineSegment(sketch, "E160.MirrorCS", {"start": v(-10.52, -24.32) * mm, "end": v(-13.68, -31.12) * mm});
            skArc(sketch, "E161.MirrorCS", {"start": v(13.68, -31.12) * mm, "mid": v(0, -34) * mm, "end": v(-13.68, -31.12) * mm});
            skArc(sketch, "E162.MirrorCS", {"start": v(15.68, -31.85) * mm, "mid": v(0, -35.5) * mm, "end": v(-15.68, -31.85) * mm});
            skLineSegment(sketch, "E163.MirrorCS", {"start": v(-11.87, -23.7) * mm, "end": v(-15.68, -31.85) * mm});
            skLineSegment(sketch, "E164.MirrorCS", {"start": v(11.87, -23.7) * mm, "end": v(15.68, -31.85) * mm});
            skLineSegment(sketch, "E165.MirrorCS", {"start": v(10.52, -24.32) * mm, "end": v(13.68, -31.12) * mm});
            skSolve(sketch);
        }
        {
            var Q0;
            Q0=makeQuery(id+"F4.imprint","IMPRINT",FACE,{"disambiguationData":[TD([[makeQuery(id+"F4.imprint","IMPRINT",EDGE,{"derivedFrom":sQuery(id+"F4.wireOp",EDGE,"E117.bottom")}),-1.0]])]});
            extrude(context, id + "F5", {"entities" : qUnion([Q0]), "operationType" : NewBodyOperationType.ADD, "depth" : 1 * mm});
        }
        {
            var Q0;
            Q0=makeQuery(id+"F5.opExtrude","CAP_EDGE",EDGE,{"disambiguationData":[OSD([sQuery(id+"F4.wireOp",EDGE,"E117.bottom")])],"isStart":false});
            var Q1;
            Q1=makeQuery(id+"F5.opExtrude","CAP_EDGE",EDGE,{"disambiguationData":[OSD([sQuery(id+"F4.wireOp",EDGE,"E125")])],"isStart":false});
            var Q2;
            Q2=makeQuery(id+"F5.opExtrude","CAP_EDGE",EDGE,{"disambiguationData":[OSD([sQuery(id+"F4.wireOp",EDGE,"E127")])],"isStart":false});
            chamfer(context, id + "F6", {"entities" : qUnion([Q0, Q1, Q2]), "width" : 1 * mm, "tangentPropagation" : true});
        }
        {
            var Q0;
            Q0=makeQuery(id+"F4.imprint","IMPRINT",FACE,{"disambiguationData":[TD([[makeQuery(id+"F4.imprint","IMPRINT",EDGE,{"derivedFrom":sQuery(id+"F4.wireOp",EDGE,"E142.0")}),-1.0]])]});
            extrude(context, id + "F7", {"entities" : qUnion([Q0]), "operationType" : NewBodyOperationType.ADD, "depth" : 1 * mm});
        }
    });
